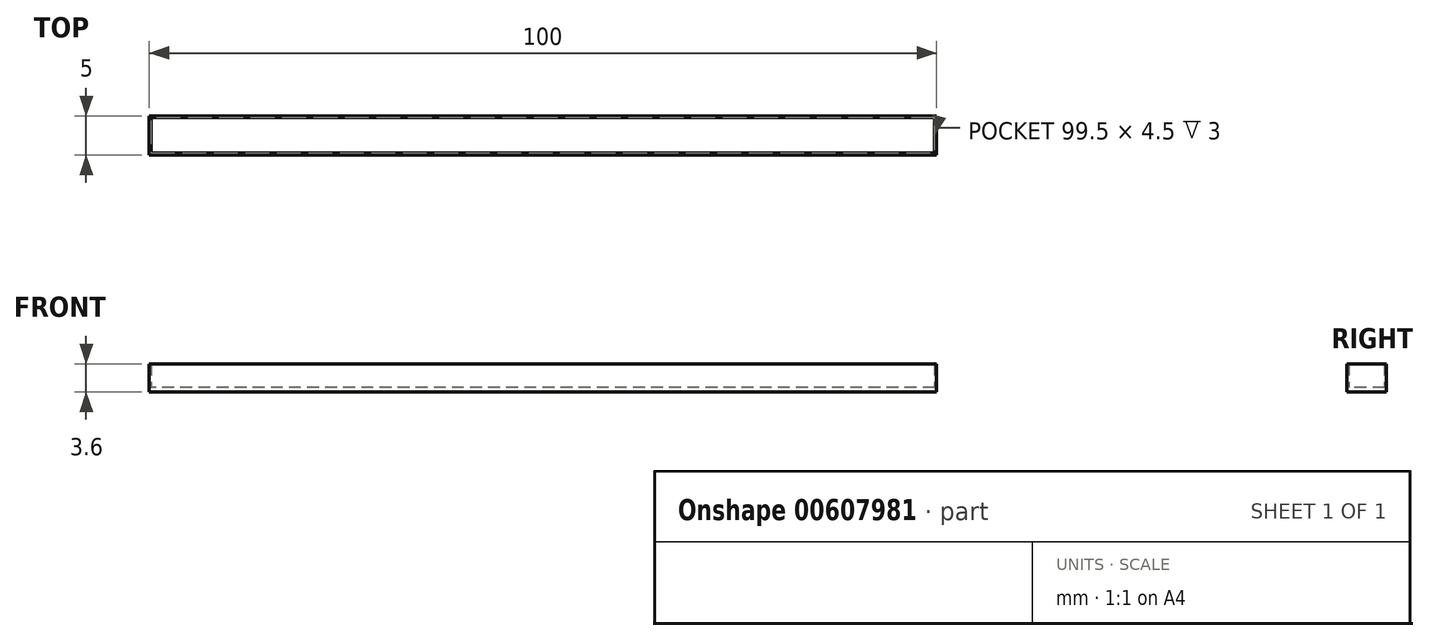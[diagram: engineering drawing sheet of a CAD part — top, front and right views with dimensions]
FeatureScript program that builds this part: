
annotation { "Feature Type Name" : "Feature", "Feature Type Description" : "" }
export const myFeature = defineFeature(function(context is Context, id is Id, definition is map)
    precondition{}
    {
        {
            var Q0;
            Q0=qCreatedBy(makeId("Top.planeOp"),FACE);
            var sketch = newSketch(context, id + "F0", { "sketchPlane" : qUnion([Q0])});
            skLineSegment(sketch, "E0.bottom", {"start": v(50, 2.5) * mm, "end": v(-50, 2.5) * mm});
            skLineSegment(sketch, "E0.top", {"start": v(50, -2.5) * mm, "end": v(-50, -2.5) * mm});
            skLineSegment(sketch, "E0.left", {"start": v(50, 2.5) * mm, "end": v(50, -2.5) * mm});
            skLineSegment(sketch, "E0.right", {"start": v(-50, 2.5) * mm, "end": v(-50, -2.5) * mm});
            skPoint(sketch, "E0.middle", {"position": v(0, 0) * mm});
            skSolve(sketch);
        }
        {
            var Q0;
            Q0=makeQuery(id+"F0.imprint","IMPRINT",FACE,{"disambiguationData":[TD([[makeQuery(id+"F0.imprint","IMPRINT",EDGE,{"derivedFrom":sQuery(id+"F0.wireOp",EDGE,"E0.bottom")}),1.0]])]});
            extrude(context, id + "F1", {"entities" : qUnion([Q0]), "depth" : .6 * mm, "offsetDistance" : 25 * mm});
        }
        {
            var Q0;
            Q0=makeQuery(id+"F1.opExtrude","CAP_FACE",FACE,{"disambiguationData":[OSD([sQuery(id+"F0.wireOp",EDGE,"E0.bottom"),sQuery(id+"F0.wireOp",EDGE,"E0.top"),sQuery(id+"F0.wireOp",EDGE,"E0.left"),sQuery(id+"F0.wireOp",EDGE,"E0.right")])],"isStart":false});
            var sketch = newSketch(context, id + "F2", { "sketchPlane" : qUnion([Q0])});
            skSolve(sketch);
        }
        {
            var Q0;
            Q0=makeQuery(id+"F2.imprint","IMPRINT",FACE,{"disambiguationData":[TD([[makeQuery(id+"F2.imprint","IMPRINT",EDGE,{"derivedFrom":makeQuery(id+"F1.opExtrude","CAP_EDGE",EDGE,{"disambiguationData":[OSD([sQuery(id+"F0.wireOp",EDGE,"E0.bottom")])],"isStart":false})}),1.0]])]});
            var sketch = newSketch(context, id + "F3", { "sketchPlane" : qUnion([Q0])});
            skLineSegment(sketch, "E1.bottom", {"start": v(49.75, 2.25) * mm, "end": v(-49.75, 2.25) * mm});
            skLineSegment(sketch, "E1.top", {"start": v(49.75, -2.25) * mm, "end": v(-49.75, -2.25) * mm});
            skLineSegment(sketch, "E1.left", {"start": v(49.75, 2.25) * mm, "end": v(49.75, -2.25) * mm});
            skLineSegment(sketch, "E1.right", {"start": v(-49.75, 2.25) * mm, "end": v(-49.75, -2.25) * mm});
            skPoint(sketch, "E1.middle", {"position": v(0, 0) * mm});
            skSolve(sketch);
        }
        {
            var Q0;
            Q0=makeQuery(id+"F2.imprint","IMPRINT",FACE,{"disambiguationData":[TD([[makeQuery(id+"F2.imprint","IMPRINT",EDGE,{"derivedFrom":makeQuery(id+"F1.opExtrude","CAP_EDGE",EDGE,{"disambiguationData":[OSD([sQuery(id+"F0.wireOp",EDGE,"E0.bottom")])],"isStart":false})}),1.0]])]});
            extrude(context, id + "F4", {"entities" : qUnion([Q0]), "operationType" : NewBodyOperationType.ADD, "depth" : 3 * mm, "offsetDistance" : 25 * mm});
        }
        {
            var Q0;
            Q0 = qSketchRegion(id + "F3", true);
            extrude(context, id + "F5", {"entities" : qUnion([Q0]), "operationType" : NewBodyOperationType.REMOVE, "depth" : 25 * mm, "offsetDistance" : 25 * mm});
        }
    });
